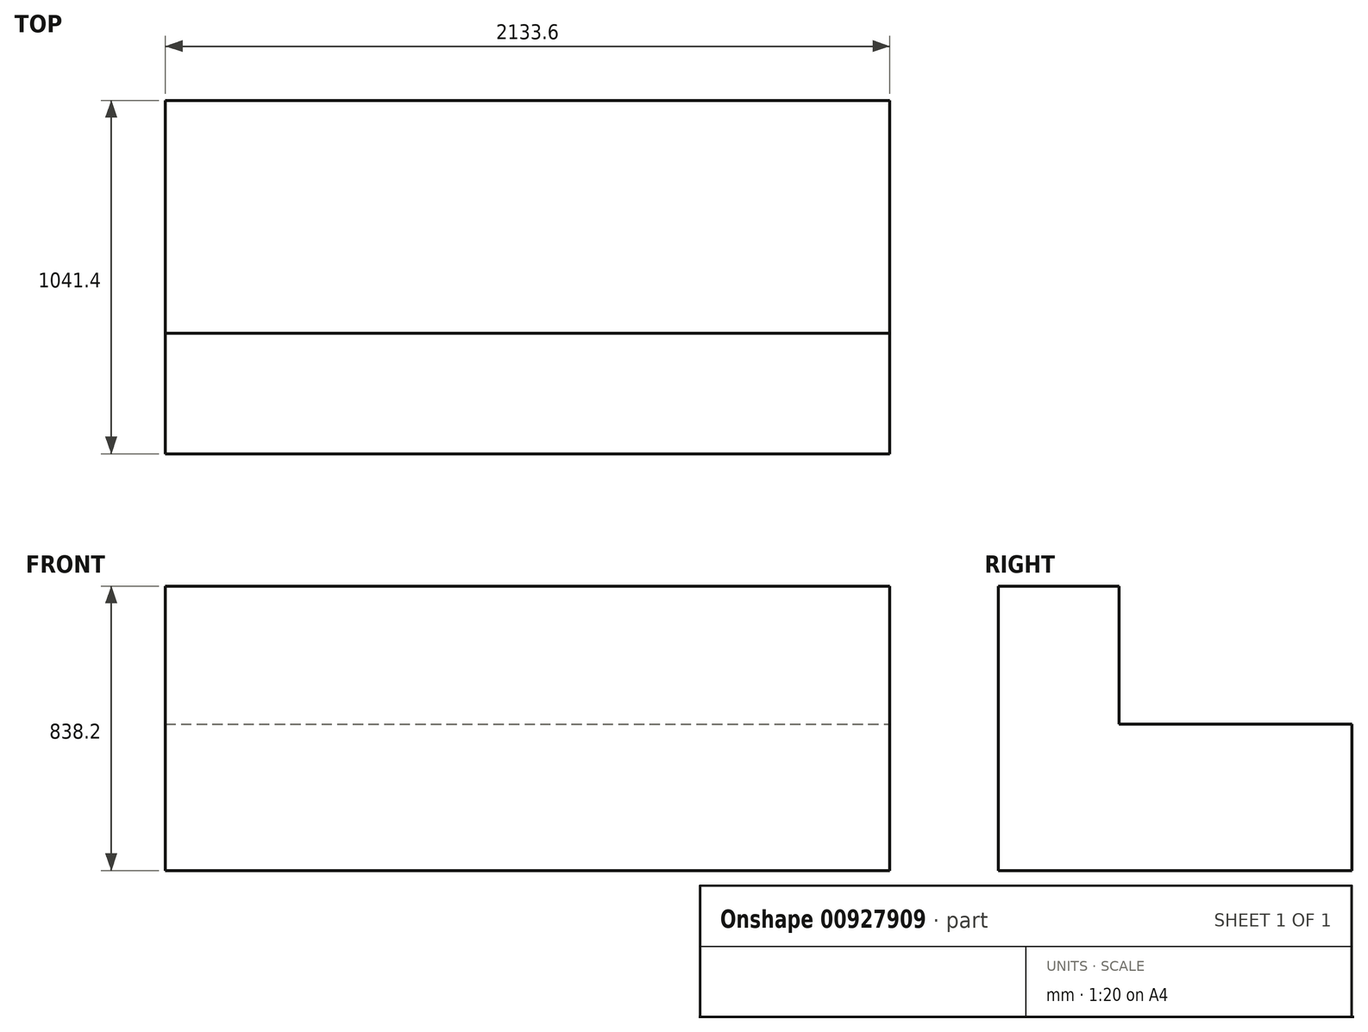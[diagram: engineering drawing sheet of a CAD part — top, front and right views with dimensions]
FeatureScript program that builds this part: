
annotation { "Feature Type Name" : "Feature", "Feature Type Description" : "" }
export const myFeature = defineFeature(function(context is Context, id is Id, definition is map)
    precondition{}
    {
        {
            var Q0;
            Q0=qCreatedBy(makeId("Top.planeOp"),FACE);
            var sketch = newSketch(context, id + "F0", { "sketchPlane" : qUnion([Q0])});
            skLineSegment(sketch, "E0.bottom", {"start": v(1066.8, 520.7) * mm, "end": v(-1066.8, 520.7) * mm});
            skLineSegment(sketch, "E0.top", {"start": v(1066.8, -520.7) * mm, "end": v(-1066.8, -520.7) * mm});
            skLineSegment(sketch, "E0.left", {"start": v(1066.8, 520.7) * mm, "end": v(1066.8, -520.7) * mm});
            skLineSegment(sketch, "E0.right", {"start": v(-1066.8, 520.7) * mm, "end": v(-1066.8, -520.7) * mm});
            skPoint(sketch, "E0.middle", {"position": v(0, 0) * mm});
            skSolve(sketch);
        }
        {
            var Q0;
            Q0 = qSketchRegion(id + "F0", true);
            extrude(context, id + "F1", {"entities" : qUnion([Q0]), "depth" : 838.2 * mm, "offsetDistance" : 25.4 * mm});
        }
        {
            var Q0;
            Q0=makeQuery(id+"F1.opExtrude","SWEPT_FACE",FACE,{"disambiguationData":[OSD([sQuery(id+"F0.wireOp",EDGE,"E0.left")])]});
            var sketch = newSketch(context, id + "F2", { "sketchPlane" : qUnion([Q0])});
            skLineSegment(sketch, "E1.bottom", {"start": v(-165.1, 431.8) * mm, "end": v(520.7, 431.8) * mm});
            skLineSegment(sketch, "E1.top", {"start": v(-165.1, 838.2) * mm, "end": v(520.7, 838.2) * mm});
            skLineSegment(sketch, "E1.left", {"start": v(-165.1, 431.8) * mm, "end": v(-165.1, 838.2) * mm});
            skLineSegment(sketch, "E1.right", {"start": v(520.7, 431.8) * mm, "end": v(520.7, 838.2) * mm});
            skSolve(sketch);
        }
        {
            var Q0;
            Q0=makeQuery(id+"F2.imprint","IMPRINT",FACE,{"disambiguationData":[TD([[makeQuery(id+"F2.imprint","IMPRINT",EDGE,{"derivedFrom":sQuery(id+"F2.wireOp",EDGE,"E1.bottom")}),1.0]])]});
            extrude(context, id + "F3", {"entities" : qUnion([Q0]), "operationType" : NewBodyOperationType.REMOVE, "endBound" : BoundingType.UP_TO_NEXT, "oppositeDirection" : true, "depth" : 25.4 * mm, "offsetDistance" : 25.4 * mm});
        }
    });
